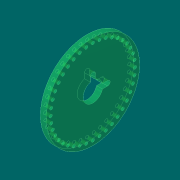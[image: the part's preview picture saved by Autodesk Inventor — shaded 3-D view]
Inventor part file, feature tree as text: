
AUTODESK INVENTOR PART (.ipt)
format: ipt  version: 2016 (Build 200138000, 138)  size: 176,640 bytes
history: native  units: mm
features: sketch x4, extrude x2, hole x2, pattern_circular x1, projected_geometry x1
ambient origin geometry x8: Origin, YZ Plane, XZ Plane, XY Plane, X Axis, Y Axis, Z Axis, Center Point
bodies: Solid1 (feature_tree)
feature tree (10):
  extrude  "Extrusion1"  Depth=5.588mm
  hole  "Hole1"  [1 undecoded]
  pattern_circular  "Circular Pattern1"  Count=40  [1 undecoded]
  hole  "Hole2"  [1 undecoded]
  extrude  "Extrusion2"  Depth=5.0mm
  sketch  "Sketch2"  dims[d7=90.0mm d8=5.588mm]
  sketch  "Sketch3"  dims[d9=0.0mm d10=40.325mm]
  projected_geometry  "Projected Loop1"
  sketch  "Sketch4"  dims[d11=3.1mm]
  sketch  "Sketch5"  dims[d12=6.0mm d13=4.0mm d14=2.0mm d15=90.0deg d16=8.0mm d17=20.594885mm d18=400.0mm d19=360.0deg d21=20.0mm d22=6.0mm d23=4.0mm d24=2.0mm d25=90.0deg d26=8.0mm d27=20.594885mm d28=5.0mm d29=5.0mm d30=15.0mm d31=15.0mm d32=10.0mm d33=0.0mm]
note: 3 required parameter values undecoded (feature->parameter linkage not recoverable at this tier; creation-order binding heuristic only, values carry confidence <= 0.55)
